AUTODESK INVENTOR PART (.ipt)
format: ipt  version: 2023 (Build 270158000, 158)  size: 191,488 bytes
history: native  units: mm
features: extrude x6, sketch x5, other x3, projected_geometry x2, fillet x1
ambient origin geometry x8: Origin, YZ Plane, XZ Plane, XY Plane, X Axis, Y Axis, Z Axis, Center Point
bodies: Body1 (feature_tree), Body2 (feature_tree), Body3 (feature_tree)
feature tree (17):
  other  "實體1"
  extrude  "擠出1"  Depth=30.0mm
  extrude  "擠出2"  Depth=3.0mm TaperAngle=0.0deg
  extrude  "擠出3"  Depth=3.0mm
  extrude  "擠出4"  Depth=9.0mm
  sketch  "草圖5"
  extrude  "擠出5"  Depth=3.0mm TaperAngle=0.0deg
  extrude  "擠出6"  Depth=20.0mm
  fillet  "圓角1"  Radius=3.0mm
  sketch  "草圖1"
  sketch  "草圖2"
  sketch  "草圖3"
  sketch  "草圖4"
  projected_geometry  "投影迴路1"
  other  "實體2"
  other  "實體3"
  projected_geometry  "投影迴路3"
